# Revit family: HR320
name_source: partatom
category: Apparecchi idraulici
units: mm (PartAtom-declared; Revit-internal decimal feet)

## family parameters
Basato su piano di lavoro = No
Condiviso = No
Mantieni orientamento annotazione = No
Numero OmniClass = 23.45.55.17
Punto di calcolo locali = No
Quota connettore circolare = Usa diametro
Sempre verticale = Sì
Taglio con vuoti quando caricato = No
Tipo di parte = Normale
Titolo OmniClass = Mixing Faucets

## types (8) — shared parameters
Commenti sul tipo = Wall mounted spout
Connessione CW = No
Connessione HW = No
Connessione di scarico = No
Connessione di ventilazione = No
Descrizione = Wall mounted spout
Produttore = IB Rubinetterie S.p.A.
URL = https://www.weareib.it
Water inlet = 10 mm  [stored 0.0328084 ft]
zero-valued in all types: Prospetto di default

## per-type parameters (varying)
| type | Finishes surface | Immagine tipo | Modello |
| Chrome | IB_Chrome | HR320CC.jpg | HR320CC |
| Antique Bronze | IB_Antique bronze | HR320BB.jpg | HR320BB |
| Pale Gold | IB_Pale gold | HR320II.jpg | HR320II |
| Brushed Gold | IB_brushed gold | HR320OS.jpg | HR320OS |
| Platinum | IB_Platinum | HR320PL.jpg | HR320PL |
| Antique Copper | IB_Antique copper | HR320RR.jpg | HR320RR |
| Rose gold | IB_Rose gold | HR320RS.jpg | HR320RS |
| Brushed Nickel | IB_Brushed nickel | HR320SS.jpg | HR320SS |

note: [stored X ft] marks values corroborated as IEEE doubles in the binary element streams (Revit-internal decimal feet)
